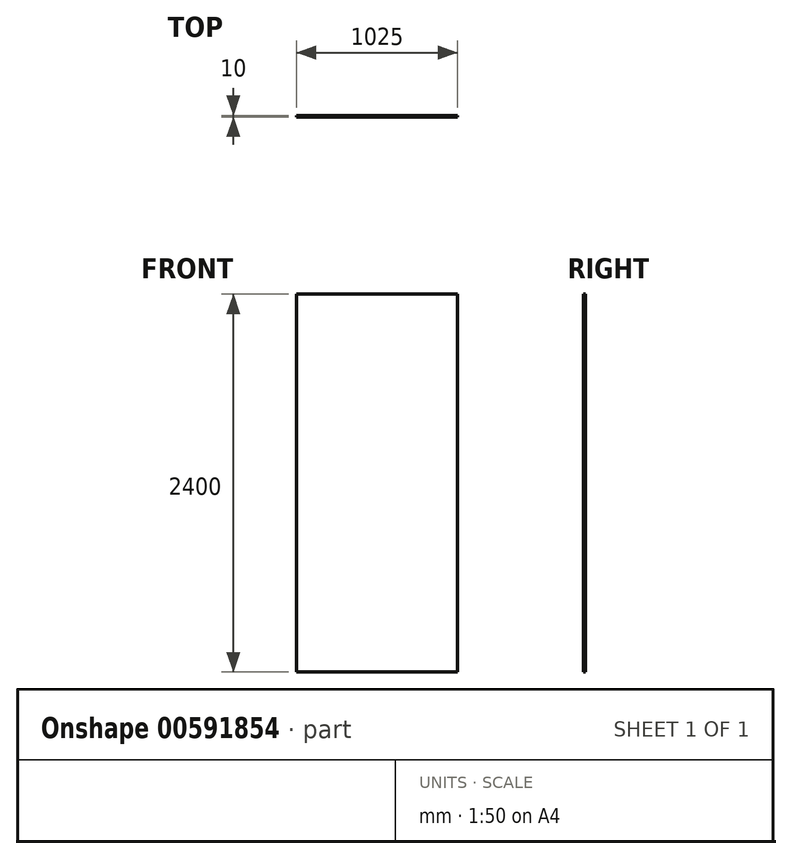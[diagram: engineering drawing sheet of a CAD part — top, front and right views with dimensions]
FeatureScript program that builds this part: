
annotation { "Feature Type Name" : "Feature", "Feature Type Description" : "" }
export const myFeature = defineFeature(function(context is Context, id is Id, definition is map)
    precondition{}
    {
        {
            var Q0;
            Q0=qCreatedBy(makeId("Front.planeOp"),FACE);
            var sketch = newSketch(context, id + "F0", { "sketchPlane" : qUnion([Q0])});
            skLineSegment(sketch, "E0.bottom", {"start": v(0, 0) * mm, "end": v(1025, 0) * mm});
            skLineSegment(sketch, "E0.top", {"start": v(0, 2400) * mm, "end": v(1025, 2400) * mm});
            skLineSegment(sketch, "E0.left", {"start": v(0, 0) * mm, "end": v(0, 2400) * mm});
            skLineSegment(sketch, "E0.right", {"start": v(1025, 0) * mm, "end": v(1025, 2400) * mm});
            skSolve(sketch);
        }
        {
            var Q0;
            Q0=makeQuery(id+"F0.imprint","IMPRINT",FACE,{"disambiguationData":[TD([[makeQuery(id+"F0.imprint","IMPRINT",EDGE,{"derivedFrom":sQuery(id+"F0.wireOp",EDGE,"E0.bottom")}),1.0]])]});
            extrude(context, id + "F1", {"entities" : qUnion([Q0]), "depth" : 10 * mm, "offsetDistance" : 25 * mm});
        }
    });
